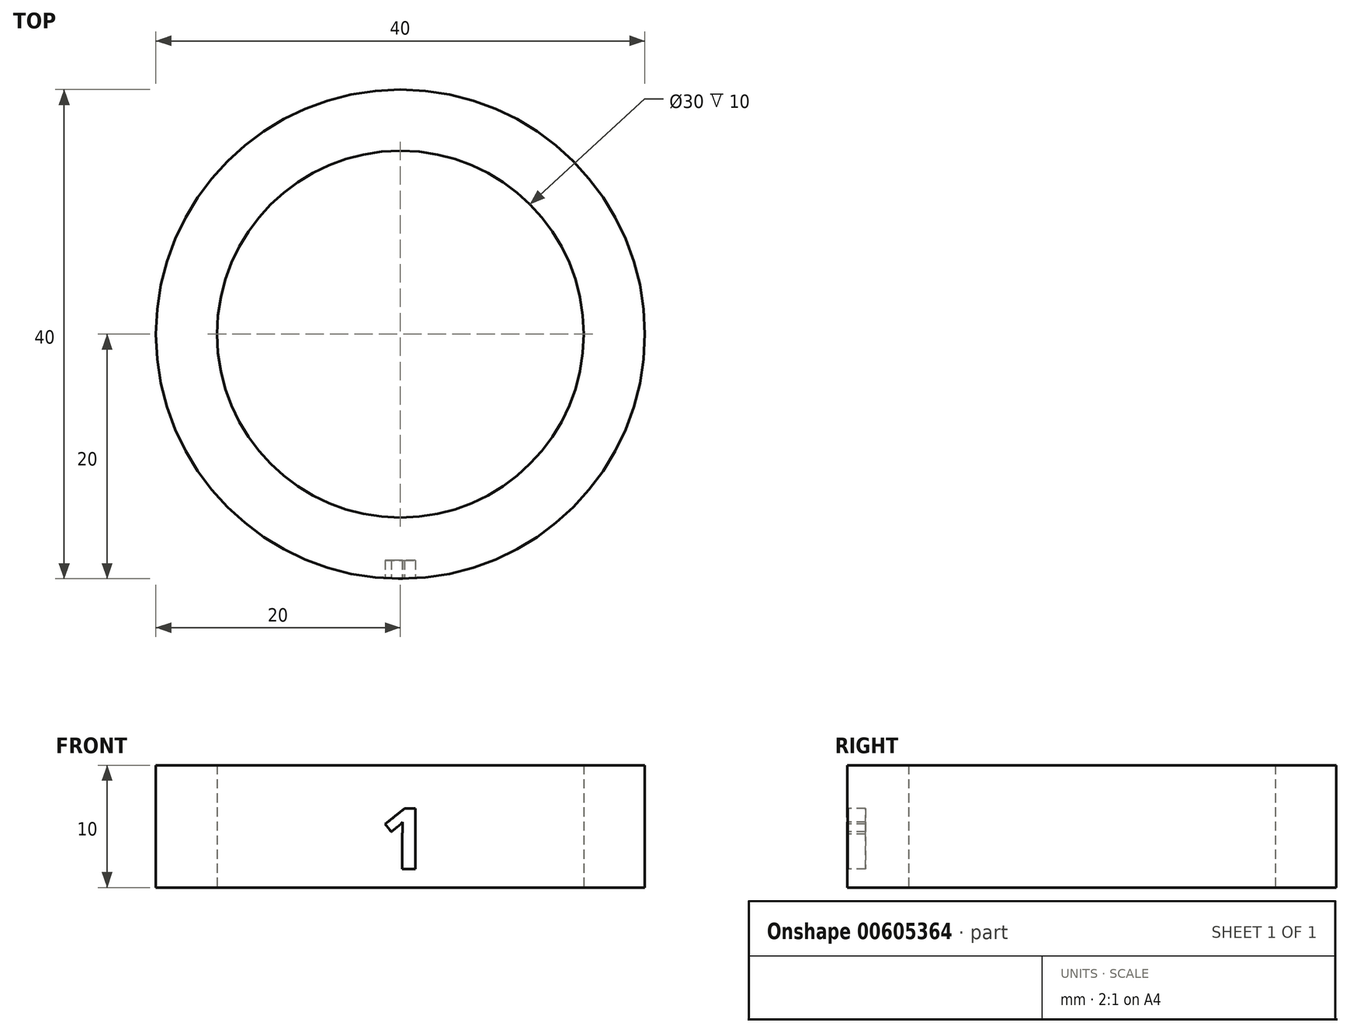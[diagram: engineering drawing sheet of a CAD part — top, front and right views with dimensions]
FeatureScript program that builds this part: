
annotation { "Feature Type Name" : "Feature", "Feature Type Description" : "" }
export const myFeature = defineFeature(function(context is Context, id is Id, definition is map)
    precondition{}
    {
        {
            var Q0;
            Q0=qCreatedBy(makeId("Top.planeOp"),FACE);
            var sketch = newSketch(context, id + "F0", { "sketchPlane" : qUnion([Q0])});
            skCircle(sketch, "E0", {"center": v(0, 0) * mm, "radius": 20 * mm});
            skCircle(sketch, "E1", {"center": v(0, 0) * mm, "radius": 15 * mm});
            skSolve(sketch);
        }
        {
            var Q0;
            Q0 = qSketchRegion(id + "F0", true);
            extrude(context, id + "F1", {"entities" : qUnion([Q0]), "depth" : 10 * mm, "offsetDistance" : 25 * mm});
        }
        {
            var Q0;
            Q0=qCreatedBy(makeId("Front.planeOp"),FACE);
            cPlane(context, id + "F2", {"entities" : qUnion([Q0]), "cplaneType" : CPlaneType.OFFSET, "offset" : 20 * mm, "width" : 150 * mm, "height" : 150 * mm});
        }
        {
            var Q0;
            Q0=qCreatedBy(id+"F2.planeOp",FACE);
            var sketch = newSketch(context, id + "F3", { "sketchPlane" : qUnion([Q0])});
            skText(sketch, "E2", { "text": "1", "fontName": "OpenSans-Bold.ttf"});
            const initialGuessF3  = {"E2": [-0.00166, 0.0015, 1, 0, 0.005]};
            skSetInitialGuess(sketch, initialGuessF3);
            skSolve(sketch);
        }
        {
            var Q0;
            Q0 = qSketchRegion(id + "F3", true);
            extrude(context, id + "F4", {"entities" : qUnion([Q0]), "operationType" : NewBodyOperationType.REMOVE, "oppositeDirection" : true, "depth" : 1.5 * mm, "offsetDistance" : 25 * mm});
        }
    });
